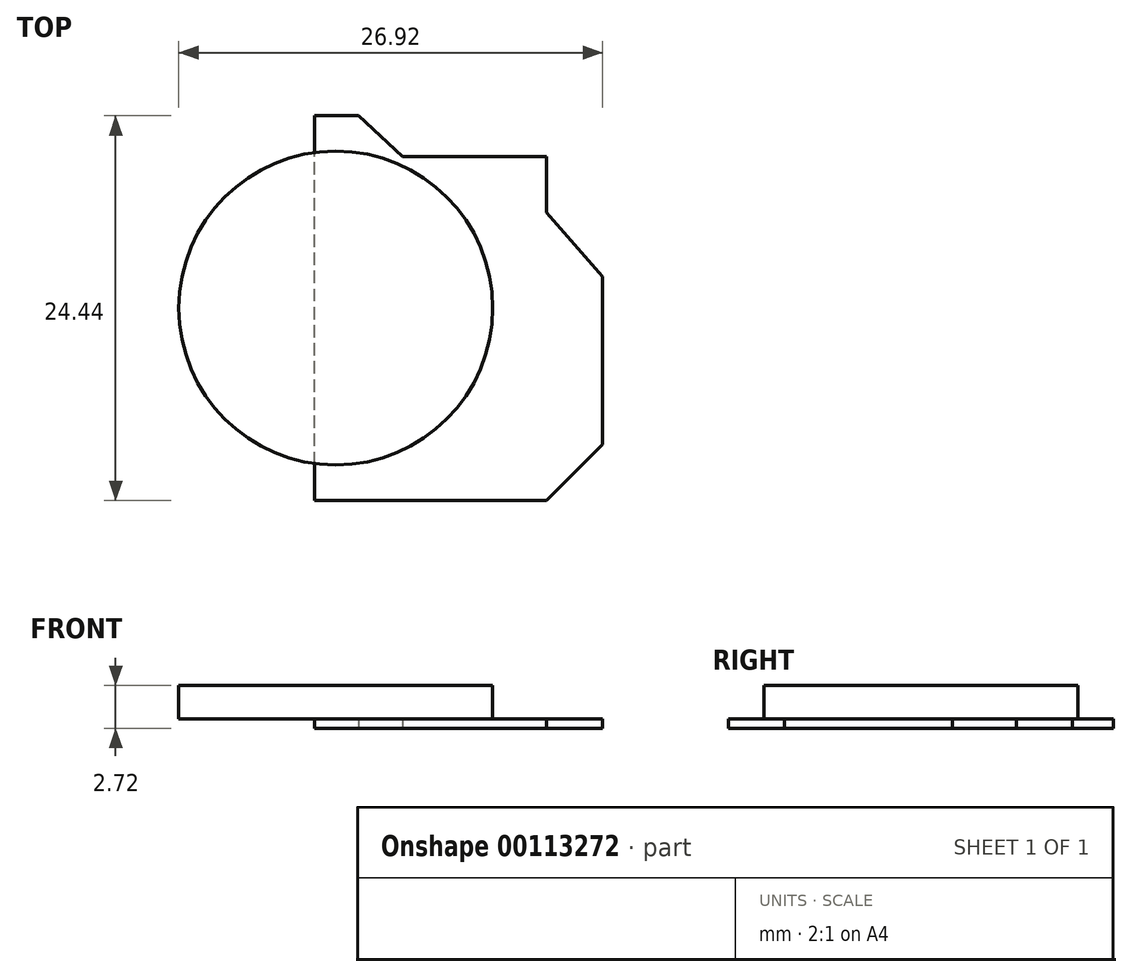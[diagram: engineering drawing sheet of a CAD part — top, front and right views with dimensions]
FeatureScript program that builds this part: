
annotation { "Feature Type Name" : "Feature", "Feature Type Description" : "" }
export const myFeature = defineFeature(function(context is Context, id is Id, definition is map)
    precondition{}
    {
        {
            var Q0;
            Q0=qCreatedBy(makeId("Top.planeOp"),FACE);
            var sketch = newSketch(context, id + "F0", { "sketchPlane" : qUnion([Q0])});
            skLineSegment(sketch, "E0.bottom", {"start": v(9.14, -12.22) * mm, "end": v(-9.14, -12.22) * mm, "construction": true});
            skLineSegment(sketch, "E0.top", {"start": v(9.14, 12.22) * mm, "end": v(-9.14, 12.22) * mm, "construction": true});
            skLineSegment(sketch, "E0.left", {"start": v(9.14, -12.22) * mm, "end": v(9.14, 12.22) * mm, "construction": true});
            skLineSegment(sketch, "E0.right", {"start": v(-9.14, -12.22) * mm, "end": v(-9.14, 12.22) * mm});
            skPoint(sketch, "E0.middle", {"position": v(0, 0) * mm});
            skCircle(sketch, "E1", {"center": v(-7.81, 0) * mm, "radius": 9.97 * mm, "construction": true});
            skLineSegment(sketch, "E2", {"start": v(9.14, 2) * mm, "end": v(9.14, -8.66) * mm});
            skLineSegment(sketch, "E3", {"start": v(-9.14, 12.22) * mm, "end": v(-6.35, 12.22) * mm});
            skLineSegment(sketch, "E4", {"start": v(-3.56, 9.63) * mm, "end": v(5.59, 9.63) * mm});
            skLineSegment(sketch, "E5", {"start": v(-9.14, -12.22) * mm, "end": v(5.59, -12.22) * mm});
            skLineSegment(sketch, "E6", {"start": v(5.59, 9.63) * mm, "end": v(5.59, 6.07) * mm});
            skLineSegment(sketch, "E7", {"start": v(5.59, -12.22) * mm, "end": v(9.14, -8.66) * mm});
            skLineSegment(sketch, "E8", {"start": v(-6.35, 12.22) * mm, "end": v(-3.56, 9.63) * mm});
            skLineSegment(sketch, "E9", {"start": v(5.59, 6.07) * mm, "end": v(9.14, 2) * mm});
            skLineSegment(sketch, "E10", {"start": v(5.59, -12.22) * mm, "end": v(9.14, -12.22) * mm, "construction": true});
            skLineSegment(sketch, "E11", {"start": v(9.14, -8.66) * mm, "end": v(9.14, -12.22) * mm, "construction": true});
            skSolve(sketch);
        }
        {
            var Q0;
            Q0=makeQuery(id+"F0.imprint","IMPRINT",FACE,{"disambiguationData":[TD([[makeQuery(id+"F0.imprint","IMPRINT",EDGE,{"derivedFrom":sQuery(id+"F0.wireOp",EDGE,"E0.right")}),-1.0]])]});
            extrude(context, id + "F1", {"entities" : qUnion([Q0]), "depth" : 0.58 * mm});
        }
        {
            var Q0;
            Q0=makeQuery(id+"F1.opExtrude","CAP_FACE",FACE,{"disambiguationData":[OSD([sQuery(id+"F0.wireOp",EDGE,"E0.right"),sQuery(id+"F0.wireOp",EDGE,"E2"),sQuery(id+"F0.wireOp",EDGE,"E3"),sQuery(id+"F0.wireOp",EDGE,"E4"),sQuery(id+"F0.wireOp",EDGE,"E5"),sQuery(id+"F0.wireOp",EDGE,"E6"),sQuery(id+"F0.wireOp",EDGE,"E7"),sQuery(id+"F0.wireOp",EDGE,"E8"),sQuery(id+"F0.wireOp",EDGE,"E9")])],"isStart":false});
            var sketch = newSketch(context, id + "F2", { "sketchPlane" : qUnion([Q0])});
            skCircle(sketch, "E12", {"center": v(-7.81, 0) * mm, "radius": 9.97 * mm});
            skSolve(sketch);
        }
        {
            var Q0;
            Q0 = qSketchRegion(id + "F2", true);
            extrude(context, id + "F3", {"entities" : qUnion([Q0]), "depth" : 2.13 * mm});
        }
        {
            var Q0;
            Q0=qCreatedBy(makeId("Top.planeOp"),FACE);
            var sketch = newSketch(context, id + "F4", { "sketchPlane" : qUnion([Q0])});
            skLineSegment(sketch, "E13.bottom", {"start": v(-18.5, -13.71) * mm, "end": v(18.5, -13.71) * mm, "construction": true});
            skLineSegment(sketch, "E13.top", {"start": v(-18.5, 13.71) * mm, "end": v(18.5, 13.71) * mm, "construction": true});
            skLineSegment(sketch, "E13.left", {"start": v(-18.5, -13.71) * mm, "end": v(-18.5, 13.71) * mm, "construction": true});
            skLineSegment(sketch, "E13.right", {"start": v(18.5, -13.71) * mm, "end": v(18.5, 13.71) * mm, "construction": true});
            skPoint(sketch, "E13.middle", {"position": v(0, 0) * mm});
            skLineSegment(sketch, "E14", {"start": v(18.5, 0) * mm, "end": v(-18.5, 0) * mm, "construction": true});
            skFitSpline(sketch, "E15", {"points": [v(-18.5, 0) * mm, v(-7.14, -13.71) * mm, v(18.5, 0) * mm, v(-7.72, 13.71) * mm, v(-18.5, 0) * mm]});
            skSolve(sketch);
        }
        {
            var Q0;
            Q0=qCreatedBy(makeId("Right.planeOp"),FACE);
            var sketch = newSketch(context, id + "F5", { "sketchPlane" : qUnion([Q0])});
            skLineSegment(sketch, "E16.bottom", {"start": v(14.9, 4.32) * mm, "end": v(-14.9, 4.32) * mm, "construction": true});
            skLineSegment(sketch, "E16.top", {"start": v(14.9, -0.85) * mm, "end": v(-14.9, -0.85) * mm, "construction": true});
            skLineSegment(sketch, "E16.left", {"start": v(14.9, 4.32) * mm, "end": v(14.9, -0.85) * mm, "construction": true});
            skLineSegment(sketch, "E16.right", {"start": v(-14.9, 4.32) * mm, "end": v(-14.9, -0.85) * mm, "construction": true});
            skFitSpline(sketch, "E17", {"points": [v(0, 4.32) * mm, v(14.9, 0.83) * mm, v(0, -0.85) * mm, v(-14.9, 0.4) * mm, v(0, 4.32) * mm]});
            skSolve(sketch);
        }
        {
            var Q0;
            Q0=makeQuery(id+"F5.imprint","IMPRINT",FACE,{"disambiguationData":[TD([[makeQuery(id+"F5.imprint","IMPRINT",EDGE,{"derivedFrom":sQuery(id+"F5.wireOp",EDGE,"E17")}),-1.0]])]});
            cPlane(context, id + "F6", {"entities" : qUnion([Q0]), "cplaneType" : CPlaneType.OFFSET, "offset" : 16.5 * mm, "width" : 152.4 * mm, "height" : 152.4 * mm});
        }
    });
